# Revit family: Control_Unit-Lutron-Vive-347_V_PowPak_Dimming_Module
name_source: partatom
category: Lighting Devices
revit_build: Autodesk Revit 2018 (Build: 20190510_1515(x64)
units: mm (PartAtom-declared; Revit-internal decimal feet)

## family parameters
Cut with Voids When Loaded = No
Host = Face
Maintain Annotation Orientation = No
OmniClass Number = 23.85.80.11.27
OmniClass Title = Lighting Controls
Part Type = Normal
Room Calculation Point = No
Round Connector Dimension = Use Diameter
Shared = No

## types (2) — shared parameters
Assembly Code = D5020
Description = Wireless Lighting Control
Finish = Plastic - Lutron - White - Matte
Frequency = 60 Hz
Instruction Sheet Link = https://www.lutron.com
Load Classification = Lighting
Manufacturer = Lutron Electronics Co., Inc
Manufacturer Fax Number = 610-282-1243
Number of Poles = 1
Overall Depth = 1.8 "
Overall Height = 4.53 "
Overall Width = 4.53 "
Performance URL = https://www.lutron.com
Power = 1 W
Product Documentation Link = https://www.lutron.com
Product Name = Vive 347 V~ Dimming Module with 0–10 V- Control
Product Page URL = https://www.lutron.com
Series = Vive
Type Comments = Junction box not provided by Lutron
URL = http://www.lutron.com
Version = 2018 - v1.0a
Video Link = https://www.youtube.com
Voltage = 347 V
Warranty URL = http://www.lutron.com
zero-valued in all types: Cost, Default Elevation

## type names (no varying parameters)
- RMJS-5T-347
- RMJS-5T-347-EM

note: column(s) folded — value = type name in every type: Model

## geometry (parser evidence)
native form markers: Blend x4, Sweep x3
no freeform markers — native parametric forms only
